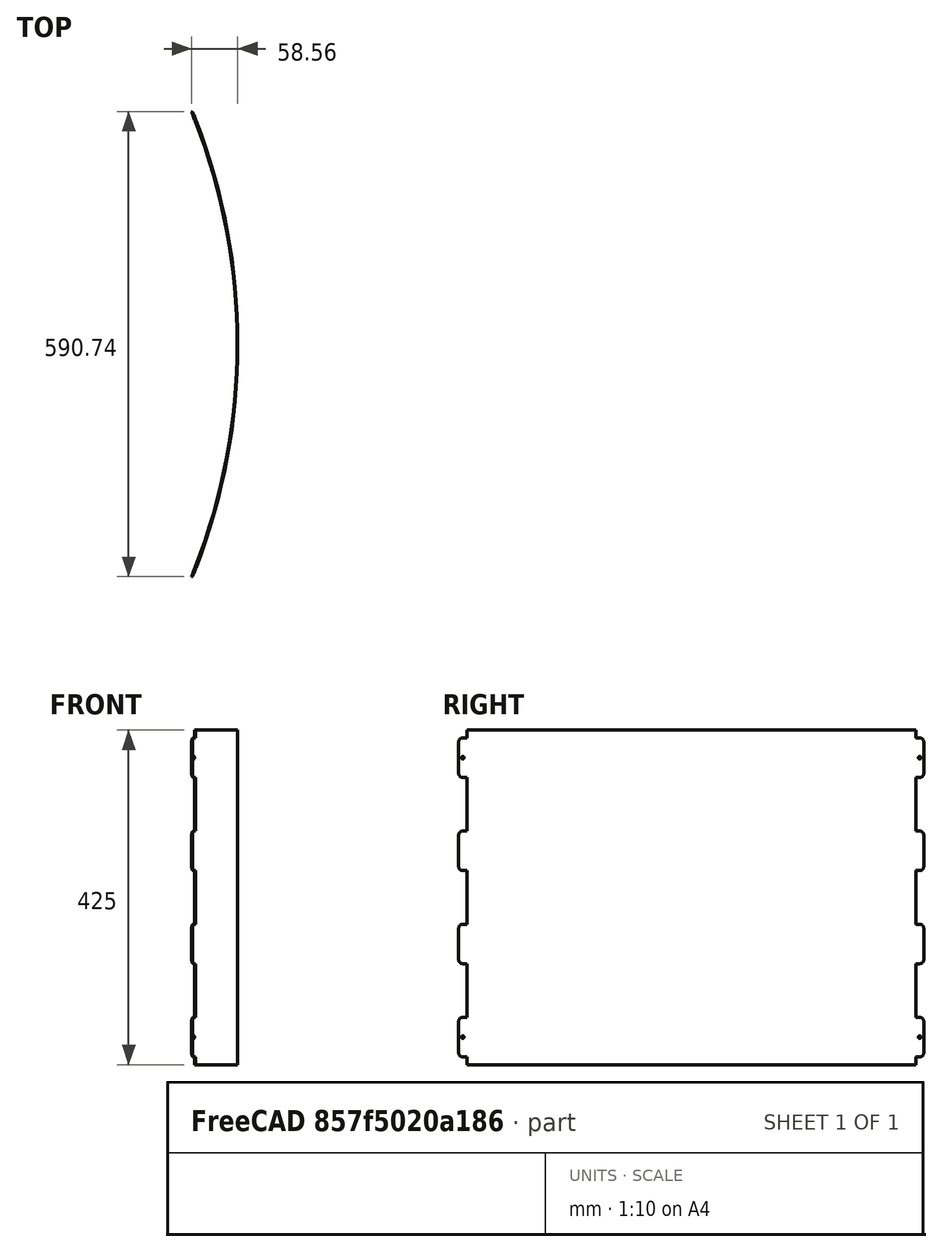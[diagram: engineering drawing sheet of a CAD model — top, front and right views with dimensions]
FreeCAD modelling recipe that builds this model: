
FCSTD DOCUMENT  (FreeCAD 1.1R38827 (Git))
Label: composit_stand3_bottom_shield_main
License: All rights reserved
LicenseURL: http://en.wikipedia.org/wiki/All_rights_reserved
objects: Sketcher::SketchObject×2, Part::FeaturePython×2, Part::Feature×1
note: 7 computed .brp shape members not serialized (recipe doc carries the construction recipe); baked Part::Feature solids carry a one-line shape summary decoded from their .brp
EXTERNAL_REF file=composit_stand3_main.FCStd obj=Sketch

FEATURE [Sketcher::SketchObject] Sketch  label="main_sketch"
  ArcFitTolerance = 0
  FullyConstrained = true
  MakeInternals = false
  expr: Constraints[5] = composit_stand3_main#<<main_sketch>>.Constraints.end_width / 2
  sketch-geometry (6):
    g0: LineSegment [constr] StartX=0 StartY=0 StartZ=0 EndX=168.8 EndY=292.37 EndZ=0
    g1: LineSegment [constr] StartX=168.8 StartY=292.37 StartZ=0 EndX=181.357 EndY=285.12 EndZ=0
    g2: LineSegment [constr] StartX=181.357 StartY=285.12 StartZ=0 EndX=174.606 EndY=302.427 EndZ=0
    g3: ArcOfCircle CenterX=-549.544 CenterY=0 CenterZ=0 NormalX=0 NormalY=0 NormalZ=1 AngleXU=0 Radius=784.545 StartAngle=0 EndAngle=0.370402
    g4: LineSegment [constr] StartX=181.357 StartY=285.12 StartZ=0 EndX=16.7432 EndY=0 EndZ=0
    g5: LineSegment [constr] StartX=181.794 StartY=283.998 StartZ=0 EndX=180.396 EndY=283.455 EndZ=0
  constraints (24):
    c: PointOnObject(g3,g-1)
    c: Coincident(g-1,g0)
    c: Coincident(g0,g1)
    c: Perpendicular(g1,g0)
    c: Angle(g0) = 1.0472
    c: Distance(g1) = 14.5
    c: PointOnObject(g2,g0)
    c: Angle(g2) = 1.94273  'angle'
    c: DistanceX(g3) = 235.001  'offset'
    c: Distance(g0) = 337.6
    c: Radius(g3) = 784.545  'r'
    c: Tangent(g2,g3)
    c: PointOnObject(g3,g-1)
    c: DistanceX(g1) = 181.357  'x'
    c: DistanceY(g1) = 285.12  'y'
    c: Coincident(g2,g1)
    c: Coincident(g1,g4)
    c: PointOnObject(g4,g-1)
    c: Parallel(g4,g0)
    c: PointOnObject(g1,g3)
    c: Coincident(g5,g3)
    c: PointOnObject(g5,g4)
    c: Perpendicular(g3,g5)
    c: Distance(g5) = 1.5
FEATURE [Part::FeaturePython] LinearArray  label="fix_placements"  # WARN: FeaturePython — macro-defined, semantics opaque (R4)
  Alignment = 0
  CellStart = A1
  Count = 4
  Dir = (0,0,1)
  DirIsDriven = true
  DistributionLaw = 0
  DrivenProperty = 1
  EndInclusive = true
  ExposePlacement = false
  GeneratorMode = 0
  MarkerShape = 1
  MarkerSize = 0
  NumElements = 4
  OrientMode = 0
  Point = (0,0,0)
  PointIsDriven = true
  Reverse = false
  SpanEnd = 390
  SpanStart = 35
  Step = 118.333
  Type = lattice2LinearArray.LinearArray
  VSGVersion = 1
  Values = 35.0 | 153.33333333333331 | 271.66666666666663 | 390.0
  ValuesSource = 2
  isLattice = 1
  expr: SpanEnd = 425 mm - SpanStart
FEATURE [Sketcher::SketchObject] Sketch001
  ArcFitTolerance = 0
  FullyConstrained = true
  MakeInternals = false
  sketch-geometry (6):
    g0: LineSegment StartX=11 StartY=0 StartZ=0 EndX=11 EndY=20 EndZ=0
    g1: LineSegment StartX=0 StartY=25 StartZ=0 EndX=0 EndY=0 EndZ=0
    g2: ArcOfCircle CenterX=6 CenterY=20 CenterZ=0 NormalX=0 NormalY=0 NormalZ=1 AngleXU=0 Radius=5 StartAngle=0 EndAngle=1.5708
    g3: GeomPoint [constr] X=11 Y=25 Z=0
    g4: LineSegment StartX=6 StartY=25 StartZ=0 EndX=0 EndY=25 EndZ=0
    g5: GeomPoint [constr] X=11 Y=-25 Z=0
  constraints (14):
    c: PointOnObject(g0,g-1)
    c: Vertical(g0)
    c: PointOnObject(g1,g-2)
    c: Coincident(g1,g-1)
    c: PointOnObject(g3,g0)
    c: Tangent(g0,g2) = -1.5708
    c: Horizontal(g4)
    c: PointOnObject(g3,g4)
    c: Tangent(g4,g2) = -1.5708
    c: Symmetric(g5,g3,g-1)
    c: DistanceY(g5,g3) = 50  'height'
    c: DistanceX(g0) = 11
    c: Radius(g2) = 5
    c: Coincident(g1,g4)
FEATURE [Part::Feature] Link008  label="sector_plexiglass_material_0.30ansi001"
  Placement = pos=(0,0,0) rot=(0,0,1;1.5708rad)
  shape: bbox 58.56 x 590.7 x 425 mm, 70 faces (baked)
FEATURE [Part::FeaturePython] Placment  label="edge_placement"  # WARN: FeaturePython — macro-defined, semantics opaque (R4)
  AttacherType = Attacher::AttachEngine3D
  ExposePlacement = true
  MarkerShape = 1
  MarkerSize = 50
  NumElements = 1
  Placement = pos=(181.357,285.12,0) rot=(0,0,1;0rad)
  Type = lattice2AttachablePlacement.AttachablePlacement
  isLattice = 1
  expr: .Placement.Base.x = <<main_sketch>>.Constraints.x
  expr: .Placement.Base.y = <<main_sketch>>.Constraints.y
